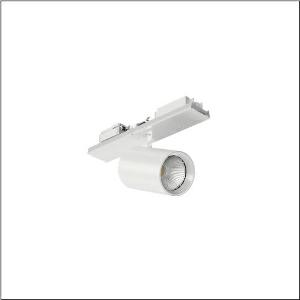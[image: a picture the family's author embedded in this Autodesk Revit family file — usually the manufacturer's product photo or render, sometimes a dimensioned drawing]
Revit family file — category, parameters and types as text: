
# Revit family: licross_r__spot_31_51sl147a43b_2678
name_source: partatom
category: Lighting Fixtures
units: mm (PartAtom-declared; Revit-internal decimal feet)

## family parameters
Cut with Voids When Loaded = No
Host = Face
Light Source = No
Part Type = Normal
Room Calculation Point = No
Round Connector Dimension = Use Diameter
Shared = No

## types (1)
- --- (1 x LED, 3720 lm, 27.9 W, 4000K)
    Apparent Load = 28 VA
    CIE Flux Codes = 93 97 100 100 100
    Color Rendering = 90
    Color Temperature = 4000K
    Default Elevation = 1800 mm
    Description = Licross® Spot 31, directional spotlight, light control with lens, of plastic, LED rated luminous flux: 3.720lm, light colour: 940, with plug, 3-pole, with phase selection, mains connection: 220..240V, AC, 50/60Hz, of aluminium, traffic white (RAL 9016), length: 140mm, diameter: 90mm, protection rating (complete): IP20, insulation class (complete): insulation class I (protective earthing), certification: CE, packaging unit: 1 piece
    Height = 175 mm
    Lamp = 1 x LED
    Lamp Light Flux = 3720 lm
    Lamp Power = 27.9 W
    Lamp count = 1
    Length = 90 mm
    Luminous efficacy = 133 lm/W
    Manufacturer = Siteco
    ModVariant = No
    Model = 51SL147A43B
    Mounting Place = Ceiling
    Mounting Type = Pendant
    Number of Poles = 1
    OnlyDefault = Yes
    Power Factor = 1
    Product Name = Licross® Spot 31
    Product group = directional spotlight
    ProductGroupID = 905
    Protection Class = Protection class I
    Protection Degree = IP 20
    RLX_Detail_Level = 1
    RLX_Emergency_Light_Flux = 0 lm
    RLX_Emergency_Type = 0
    RLX_Emergency_Type_DB = No
    RlxData = <blob elided: 14849 chars, md5=5a8fc799>
    Socket = socket
    Standby Power = 0 W
    System Light Flux = 3720 lm
    System Power = 28 W
    Type Comments = factory setting: luminous flux: 100 % | (ON | ON | ON) | 700 mA
    Type Image = l_1245720.jpg
    URL = http://relux.com
    VarID = @adj_063735
    Voltage = 0 V
    Weight = 0.00 kg
    Width = 0 mm  [stored 0 ft]

note: [stored X ft] marks values corroborated as IEEE doubles in the binary element streams (Revit-internal decimal feet)

## geometry (parser evidence)
native form markers: Sweep x10
no freeform markers — native parametric forms only
